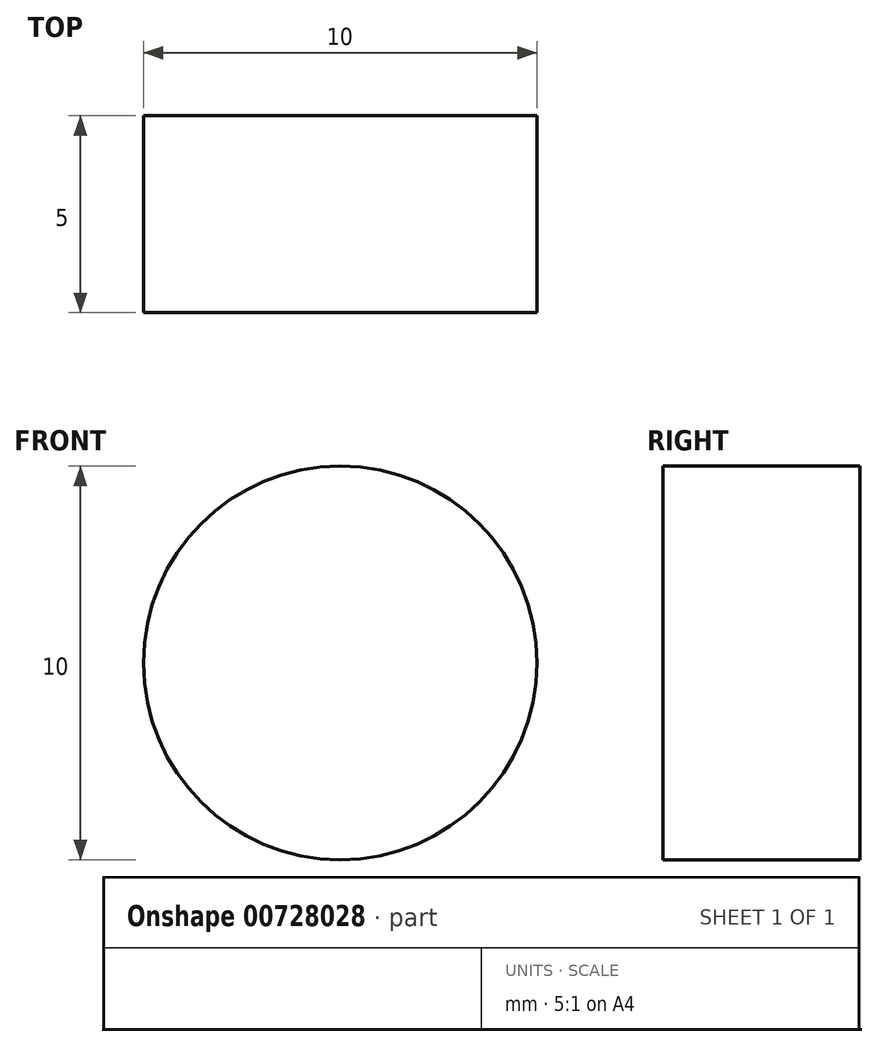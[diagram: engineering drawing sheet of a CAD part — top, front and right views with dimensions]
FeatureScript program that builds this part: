
annotation { "Feature Type Name" : "Feature", "Feature Type Description" : "" }
export const myFeature = defineFeature(function(context is Context, id is Id, definition is map)
    precondition{}
    {
        {
            var Q0;
            Q0=qCreatedBy(makeId("Front.planeOp"),FACE);
            var sketch = newSketch(context, id + "F0", { "sketchPlane" : qUnion([Q0])});
            skCircle(sketch, "E0", {"center": v(0, 0) * mm, "radius": 5 * mm});
            skSolve(sketch);
        }
        {
            var Q0;
            Q0 = qSketchRegion(id + "F0", true);
            extrude(context, id + "F1", {"entities" : qUnion([Q0]), "endBound" : BoundingType.SYMMETRIC, "depth" : 5 * mm, "offsetDistance" : 25 * mm});
        }
    });
